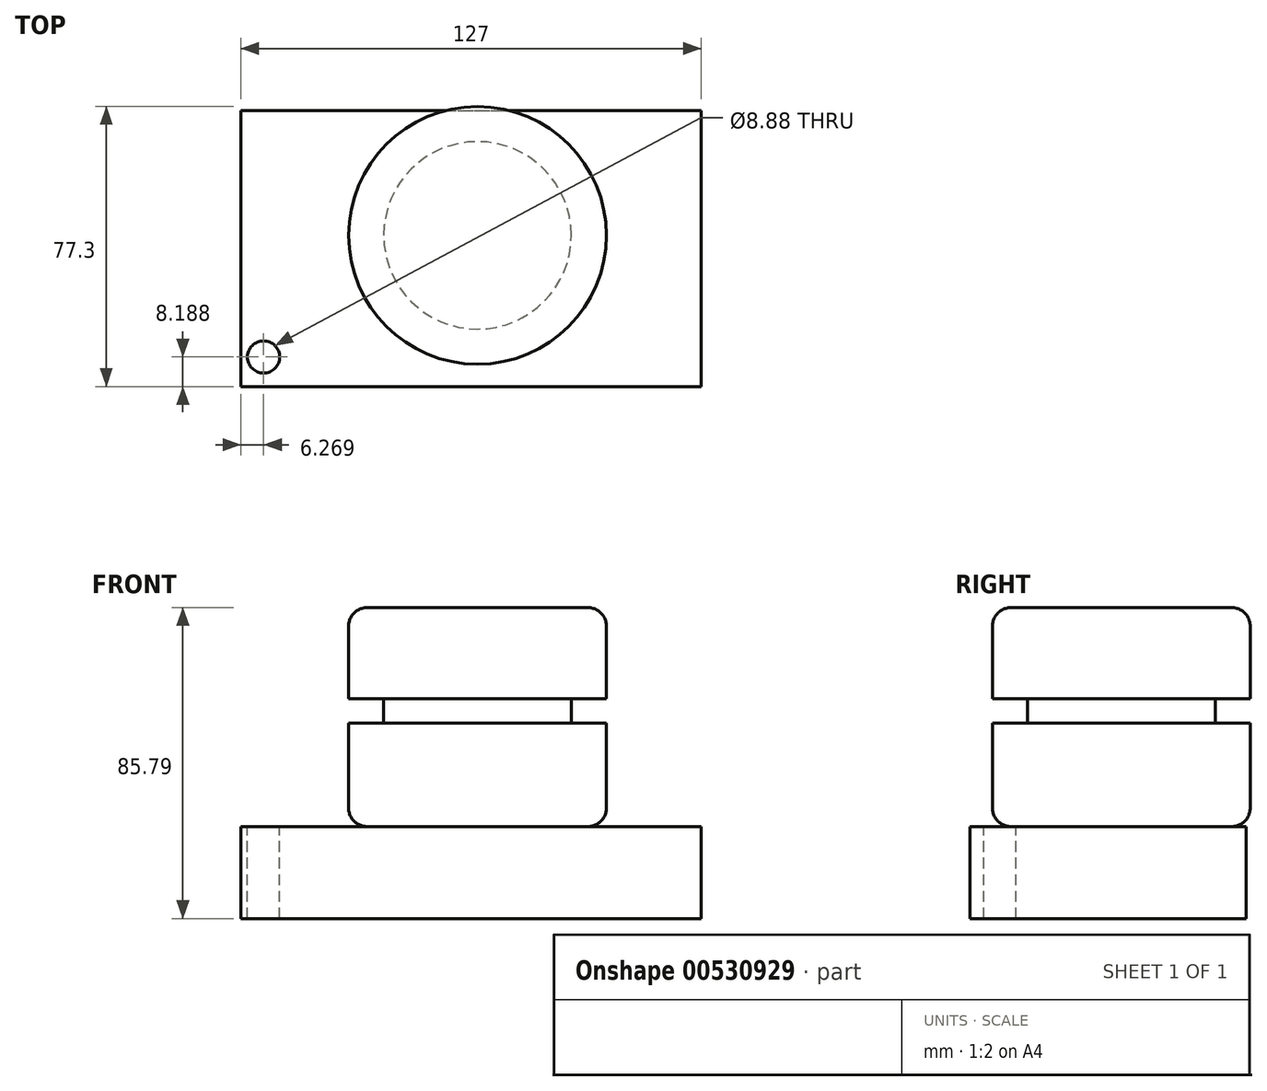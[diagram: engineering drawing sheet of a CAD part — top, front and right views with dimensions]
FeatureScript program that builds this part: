
annotation { "Feature Type Name" : "Feature", "Feature Type Description" : "" }
export const myFeature = defineFeature(function(context is Context, id is Id, definition is map)
    precondition{}
    {
        {
            var Q0;
            Q0=qCreatedBy(makeId("Top.planeOp"),FACE);
            var sketch = newSketch(context, id + "F0", { "sketchPlane" : qUnion([Q0])});
            skLineSegment(sketch, "E0.bottom", {"start": v(-65.3, 34.46) * mm, "end": v(61.7, 34.46) * mm});
            skLineSegment(sketch, "E0.top", {"start": v(-65.3, -41.74) * mm, "end": v(61.7, -41.74) * mm});
            skLineSegment(sketch, "E0.left", {"start": v(-65.3, 34.46) * mm, "end": v(-65.3, -41.74) * mm});
            skLineSegment(sketch, "E0.right", {"start": v(61.7, 34.46) * mm, "end": v(61.7, -41.74) * mm});
            skSolve(sketch);
        }
        {
            var Q0;
            Q0=makeQuery(id+"F0.imprint","IMPRINT",FACE,{"disambiguationData":[TD([[makeQuery(id+"F0.imprint","IMPRINT",EDGE,{"derivedFrom":sQuery(id+"F0.wireOp",EDGE,"E0.bottom")}),-1.0]])]});
            extrude(context, id + "F1", {"entities" : qUnion([Q0]), "depth" : 25.4 * mm, "offsetDistance" : 25.4 * mm});
        }
        {
            var Q0;
            Q0=makeQuery(id+"F1.opExtrude","CAP_FACE",FACE,{"disambiguationData":[OSD([sQuery(id+"F0.wireOp",EDGE,"E0.bottom"),sQuery(id+"F0.wireOp",EDGE,"E0.top"),sQuery(id+"F0.wireOp",EDGE,"E0.left"),sQuery(id+"F0.wireOp",EDGE,"E0.right")])],"isStart":false});
            var sketch = newSketch(context, id + "F2", { "sketchPlane" : qUnion([Q0])});
            skCircle(sketch, "E1", {"center": v(-59.03, -33.55) * mm, "radius": 4.44 * mm});
            skSolve(sketch);
        }
        {
            var Q0;
            Q0=makeQuery(id+"F2.imprint","IMPRINT",FACE,{"disambiguationData":[TD([[makeQuery(id+"F2.imprint","IMPRINT",EDGE,{"derivedFrom":sQuery(id+"F2.wireOp",EDGE,"E1")}),1.0]])]});
            var Q1;
            Q1=sQuery(id+"F2.wireOp",EDGE,"E1");
            extrude(context, id + "F3", {"entities" : qUnion([Q0]), "operationType" : NewBodyOperationType.REMOVE, "surfaceEntities" : qUnion([Q1]), "endBound" : BoundingType.THROUGH_ALL, "oppositeDirection" : true, "depth" : 25.4 * mm, "offsetDistance" : 25.4 * mm});
        }
        {
            var Q0;
            Q0=qCreatedBy(makeId("Front.planeOp"),FACE);
            var sketch = newSketch(context, id + "F4", { "sketchPlane" : qUnion([Q0])});
            skLineSegment(sketch, "E2.bottom", {"start": v(0, 25.4) * mm, "end": v(35.56, 25.4) * mm});
            skLineSegment(sketch, "E2.top", {"start": v(0, 85.8) * mm, "end": v(35.56, 85.8) * mm});
            skLineSegment(sketch, "E2.left", {"start": v(0, 25.4) * mm, "end": v(0, 85.8) * mm});
            skLineSegment(sketch, "E2.right", {"start": v(35.56, 25.4) * mm, "end": v(35.56, 85.8) * mm});
            skLineSegment(sketch, "E3.left", {"start": v(0, 85.8) * mm, "end": v(0, 85.8) * mm});
            skSolve(sketch);
        }
        {
            var Q0;
            Q0 = qSketchRegion(id + "F4", true);
            var Q1;
            Q1=sQuery(id+"F4.wireOp",EDGE,"E2.left");
            revolve(context, id + "F5", {"entities" : qUnion([Q0]), "axis" : qUnion([Q1]), "revolveType" : RevolveType.FULL});
        }
        {
            var Q0;
            Q0=qCreatedBy(makeId("Front.planeOp"),FACE);
            var sketch = newSketch(context, id + "F6", { "sketchPlane" : qUnion([Q0])});
            skLineSegment(sketch, "E4.right", {"start": v(25.87, 60.72) * mm, "end": v(25.87, 53.9) * mm});
            skLineSegment(sketch, "E5", {"start": v(25.87, 60.72) * mm, "end": v(35.63, 60.72) * mm});
            skLineSegment(sketch, "E6", {"start": v(25.87, 53.9) * mm, "end": v(35.63, 53.9) * mm});
            skLineSegment(sketch, "E7", {"start": v(35.63, 60.72) * mm, "end": v(35.63, 53.9) * mm});
            skSolve(sketch);
        }
        {
            var Q0;
            Q0=qCreatedBy(makeId("Right.planeOp"),FACE);
            var sketch = newSketch(context, id + "F7", { "sketchPlane" : qUnion([Q0])});
            skLineSegment(sketch, "E8", {"start": v(0, 0) * mm, "end": v(0, 74.58) * mm});
            skSolve(sketch);
        }
        {
            var Q0;
            Q0 = qSketchRegion(id + "F6", true);
            var Q1;
            Q1=sQuery(id+"F7.wireOp",EDGE,"E8");
            revolve(context, id + "F8", {"operationType" : NewBodyOperationType.REMOVE, "entities" : qUnion([Q0]), "axis" : qUnion([Q1]), "revolveType" : RevolveType.FULL, "oppositeDirection" : true});
        }
        {
            var Q0;
            Q0=makeQuery(id+"F5.opRevolve","SWEPT_EDGE",EDGE,{"disambiguationData":[OSD([sQuery(id+"F4.wireOp",EDGE,"E2.top"),sQuery(id+"F4.wireOp",EDGE,"E2.right")])]});
            fillet(context, id + "F9", {"entities" : qUnion([Q0]), "radius" : 5.08 * mm, "tangentPropagation" : true, "allowEdgeOverflow" : false});
        }
        {
            var Q0;
            Q0=makeQuery(id+"F5.opRevolve","SWEPT_EDGE",EDGE,{"disambiguationData":[OSD([sQuery(id+"F4.wireOp",EDGE,"E2.bottom"),sQuery(id+"F4.wireOp",EDGE,"E2.right")])]});
            fillet(context, id + "F10", {"entities" : qUnion([Q0]), "radius" : 5.08 * mm, "tangentPropagation" : true, "allowEdgeOverflow" : false});
        }
    });
